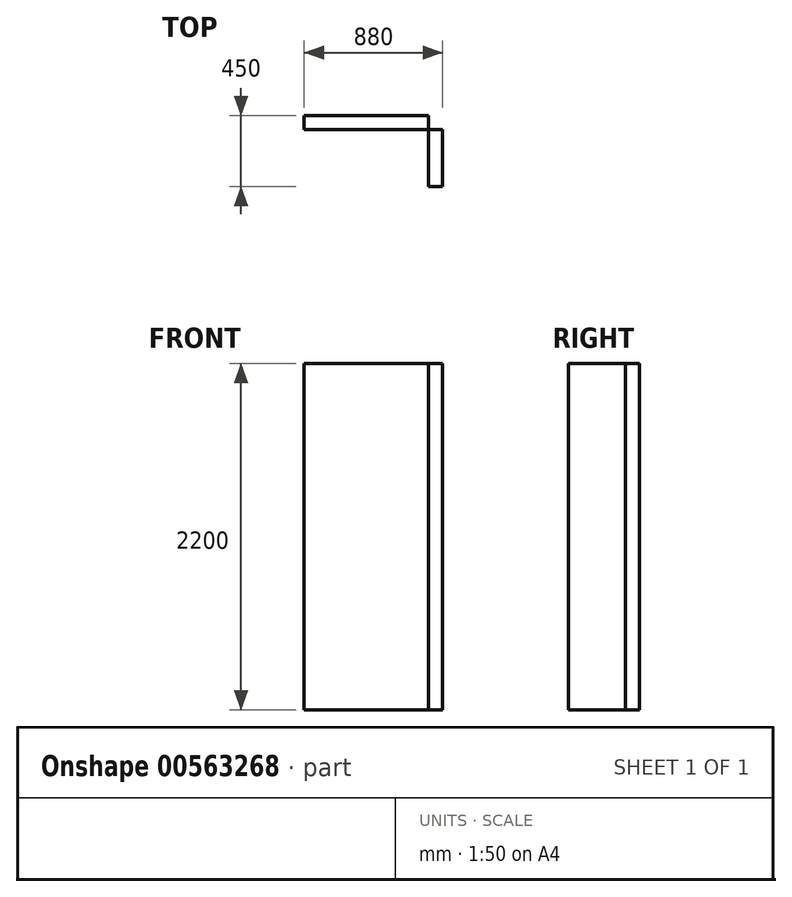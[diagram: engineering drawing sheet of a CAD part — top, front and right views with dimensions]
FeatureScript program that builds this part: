
annotation { "Feature Type Name" : "Feature", "Feature Type Description" : "" }
export const myFeature = defineFeature(function(context is Context, id is Id, definition is map)
    precondition{}
    {
        {
            var Q0;
            Q0=qCreatedBy(makeId("Front.planeOp"),FACE);
            var sketch = newSketch(context, id + "F0", { "sketchPlane" : qUnion([Q0])});
            skLineSegment(sketch, "E0.bottom", {"start": v(-394.58, 1514.5) * mm, "end": v(395.42, 1514.5) * mm});
            skLineSegment(sketch, "E0.top", {"start": v(-394.58, -685.5) * mm, "end": v(395.42, -685.5) * mm});
            skLineSegment(sketch, "E0.left", {"start": v(-394.58, 1514.5) * mm, "end": v(-394.58, -685.5) * mm});
            skLineSegment(sketch, "E0.right", {"start": v(395.42, 1514.5) * mm, "end": v(395.42, -685.5) * mm});
            skSolve(sketch);
        }
        {
            var Q0;
            Q0 = qSketchRegion(id + "F0", true);
            extrude(context, id + "F1", {"entities" : qUnion([Q0]), "oppositeDirection" : true, "depth" : 90 * mm, "offsetDistance" : 25 * mm});
        }
        {
            var Q0;
            Q0=makeQuery(id+"F1.opExtrude","SWEPT_FACE",FACE,{"disambiguationData":[OSD([sQuery(id+"F0.wireOp",EDGE,"E0.right")])]});
            var sketch = newSketch(context, id + "F2", { "sketchPlane" : qUnion([Q0])});
            skSolve(sketch);
        }
        {
            var Q0;
            {var subQ0=sQuery(id+"F0.wireOp",EDGE,"E0.right");Q0=makeQuery(id+"F2.imprint","IMPRINT",FACE,{"disambiguationData":[TD([[makeQuery(id+"F2.imprint","IMPRINT",EDGE,{"derivedFrom":makeQuery(id+"F1.opExtrude","CAP_EDGE",EDGE,{"disambiguationData":[OSD([subQ0])],"isStart":true})}),1.0]])]});}
            var sketch = newSketch(context, id + "F3", { "sketchPlane" : qUnion([Q0])});
            skLineSegment(sketch, "E1.bottom", {"start": v(0, 1514.5) * mm, "end": v(-360, 1514.5) * mm});
            skLineSegment(sketch, "E1.top", {"start": v(0, -685.5) * mm, "end": v(-360, -685.5) * mm});
            skLineSegment(sketch, "E1.left", {"start": v(0, 1514.5) * mm, "end": v(0, -685.5) * mm});
            skLineSegment(sketch, "E1.right", {"start": v(-360, 1514.5) * mm, "end": v(-360, -685.5) * mm});
            skSolve(sketch);
        }
        {
            var Q0;
            Q0=makeQuery(id+"F3.imprint","IMPRINT",FACE,{"disambiguationData":[TD([[makeQuery(id+"F3.imprint","IMPRINT",EDGE,{"derivedFrom":sQuery(id+"F3.wireOp",EDGE,"E1.bottom")}),1.0]])]});
            extrude(context, id + "F4", {"entities" : qUnion([Q0]), "depth" : 90 * mm, "offsetDistance" : 25 * mm});
        }
    });
